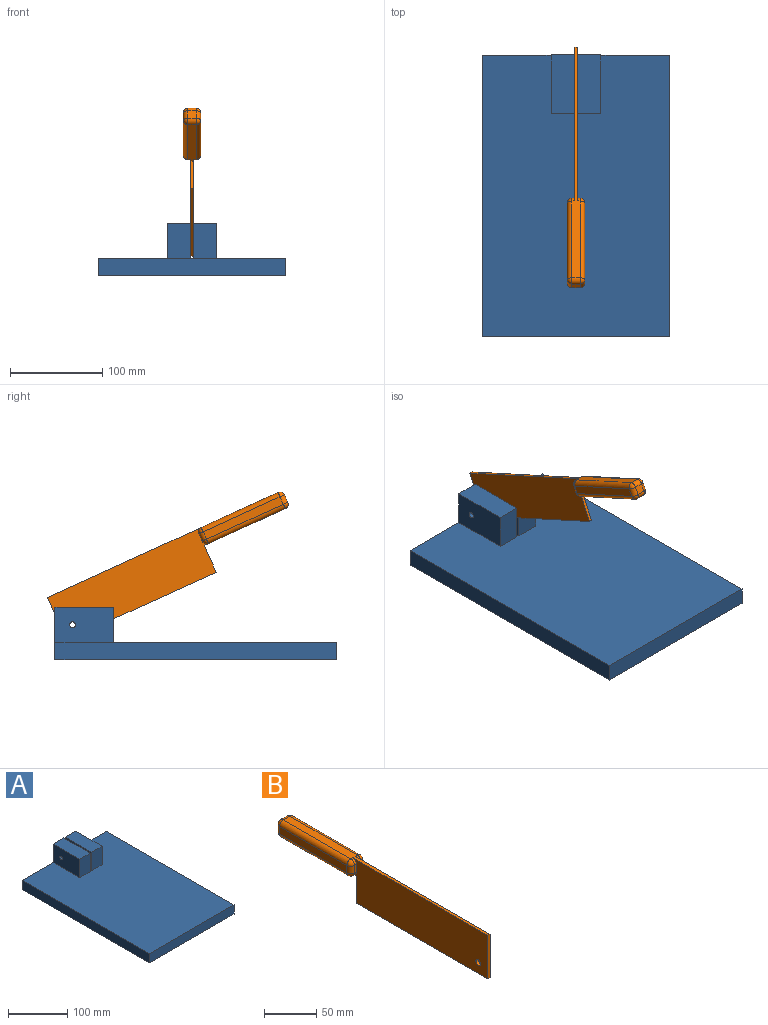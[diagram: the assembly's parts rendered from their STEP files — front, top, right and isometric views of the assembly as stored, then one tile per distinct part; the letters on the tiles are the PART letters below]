
ASSEMBLY  parts=2 mates=1
PART A: 16 faces, bbox 203.2x304.8x57.2 mm
  f0: plane 304.8x203.2mm, normal (0,0,1), area 58709.6mm2, adj f1,f2,f3,f4,f6,f7,f8,f10
  f1: plane 304.8x19.05mm, normal (1,0,0), area 5806.4mm2, adj f0,f2,f4,f5
  f2: plane 203.2x57.15mm, normal (0,1,0), area 5806.4mm2, adj f0,f1,f3,f5,f6,f7,f9,f10
  f3: plane 304.8x19.05mm, normal (-1,0,0), area 5806.4mm2, adj f0,f2,f4,f5
  f4: plane 203.2x19.05mm, normal (0,-1,0), area 3871mm2, adj f0,f1,f3,f5
  f5: plane 304.8x203.2mm, normal (0,0,-1), area 61935.4mm2, adj f1,f2,f3,f4
  f6: plane 63.5x38.1mm, normal (1,0,0), area 2387.7mm2, adj f0,f2,f8,f9,f15
  f7: plane 63.5x38.1mm, normal (-1,0,0), area 2387.7mm2, adj f0,f2,f8,f9,f15
  f8: plane 38.1x25.4mm, normal (0,-1,0), area 967.7mm2, adj f0,f6,f7,f9
  f9: plane 63.5x25.4mm, normal (0,0,1), area 1612.9mm2, adj f2,f6,f7,f8
  f10: plane 63.5x38.1mm, normal (-1,0,0), area 2387.7mm2, adj f0,f2,f11,f13,f14
  f11: plane 38.1x25.4mm, normal (0,-1,0), area 967.7mm2, adj f0,f10,f12,f13
  f12: plane 63.5x38.1mm, normal (1,0,0), area 2387.7mm2, adj f0,f2,f11,f13,f14
  f13: plane 63.5x25.4mm, normal (0,0,1), area 1612.9mm2, adj f2,f10,f11,f12
  f14: cylinder r=3.17mm len=25.4mm, axis (-1,0,0), area 506.7mm2, adj f10,f12
  f15: cylinder r=3.17mm len=25.4mm, axis (-1,0,0), area 506.7mm2, adj f6,f7
PART B: 35 faces, bbox 19.1x279.4x50.8 mm
  f0: plane 31.75x3.18mm, normal (0,1,0), area 100.8mm2, adj f1,f4,f5,f7
  f1: plane 177.8x3.18mm, normal (0,0,-1), area 564.5mm2, adj f0,f3,f4,f5
  f2: plane 274.32x8.89mm, normal (0,0,1), area 1393.5mm2, adj f3,f4,f5,f25,f27,f29,f31,f33
  f3: plane 50.8x3.18mm, normal (0,-1,0), area 161.3mm2, adj f1,f2,f4,f5
  f4: plane 182.88x50.8mm, normal (1,0,0), area 9011.6mm2, adj f0,f1,f2,f3,f6,f7,f16,f25
  f5: plane 182.88x50.8mm, normal (-1,0,0), area 9011.6mm2, adj f0,f1,f2,f3,f7,f9,f24,f33
  f6: plane 8.89x2.86mm, normal (0,-1,0), area 25.4mm2, adj f4,f15,f16,f25
  f7: plane 96.52x8.89mm, normal (0,0,-1), area 829mm2, adj f0,f4,f5,f16,f18,f20,f22,f24
  f8: plane 8.89x8.89mm, normal (0,1,0), area 79mm2, adj f12,f14,f20,f29
  f9: plane 8.89x2.86mm, normal (0,-1,0), area 25.4mm2, adj f5,f13,f24,f33
  f10: plane 91.44x8.89mm, normal (1,0,0), area 812.9mm2, adj f14,f15,f18,f27
  f11: plane 91.44x8.89mm, normal (-1,0,0), area 812.9mm2, adj f12,f13,f22,f31
  f12: cylinder r=5.08mm len=8.89mm, axis (0,0,1), area 70.9mm2, adj f8,f11,f21,f30
  f13: cylinder r=5.08mm len=8.89mm, axis (0,0,-1), area 70.9mm2, adj f9,f11,f23,f32
  f14: cylinder r=5.08mm len=8.89mm, axis (0,0,-1), area 70.9mm2, adj f8,f10,f19,f28
  f15: cylinder r=5.08mm len=8.89mm, axis (0,0,1), area 70.9mm2, adj f6,f10,f17,f26
  f16: cylinder r=5.08mm len=5.08mm, axis (-1,0,0), area 22.8mm2, adj f4,f6,f7,f17
  f17: sphere r=5.08mm, area 40.5mm2, adj f15,f16,f18
  f18: cylinder r=5.08mm len=91.44mm, axis (0,-1,0), area 729.7mm2, adj f7,f10,f17,f19
  f19: sphere r=5.08mm, area 40.5mm2, adj f14,f18,f20
  f20: cylinder r=5.08mm len=8.89mm, axis (1,0,0), area 70.9mm2, adj f7,f8,f19,f21
  f21: sphere r=5.08mm, area 40.5mm2, adj f12,f20,f22
  f22: cylinder r=5.08mm len=91.44mm, axis (0,1,0), area 729.7mm2, adj f7,f11,f21,f23
  f23: sphere r=5.08mm, area 40.5mm2, adj f13,f22,f24
  f24: cylinder r=5.08mm len=5.08mm, axis (-1,0,0), area 22.8mm2, adj f5,f7,f9,f23
  f25: cylinder r=5.08mm len=5.08mm, axis (1,0,0), area 22.8mm2, adj f2,f4,f6,f26
  f26: sphere r=5.08mm, area 40.5mm2, adj f15,f25,f27
  f27: cylinder r=5.08mm len=91.44mm, axis (0,1,0), area 729.7mm2, adj f2,f10,f26,f28
  f28: sphere r=5.08mm, area 40.5mm2, adj f14,f27,f29
  f29: cylinder r=5.08mm len=8.89mm, axis (-1,0,0), area 70.9mm2, adj f2,f8,f28,f30
  f30: sphere r=5.08mm, area 40.5mm2, adj f12,f29,f31
  f31: cylinder r=5.08mm len=91.44mm, axis (0,-1,0), area 729.7mm2, adj f2,f11,f30,f32
  f32: sphere r=5.08mm, area 40.5mm2, adj f13,f31,f33
  f33: cylinder r=5.08mm len=5.08mm, axis (1,0,0), area 22.8mm2, adj f2,f5,f9,f32
  f34: cylinder r=3.17mm len=6.35mm, axis (1,0,0), area 63.3mm2, adj f4,f5
PLACE A at identity
PLACE B rot(axis=(0,-0.21,-0.98),180deg) t=(0,69.26,81.23)mm
MATE revolute B.f34 <-> A.f14  axis (1,0,0) through (1.59,133.35,38.1)mm
